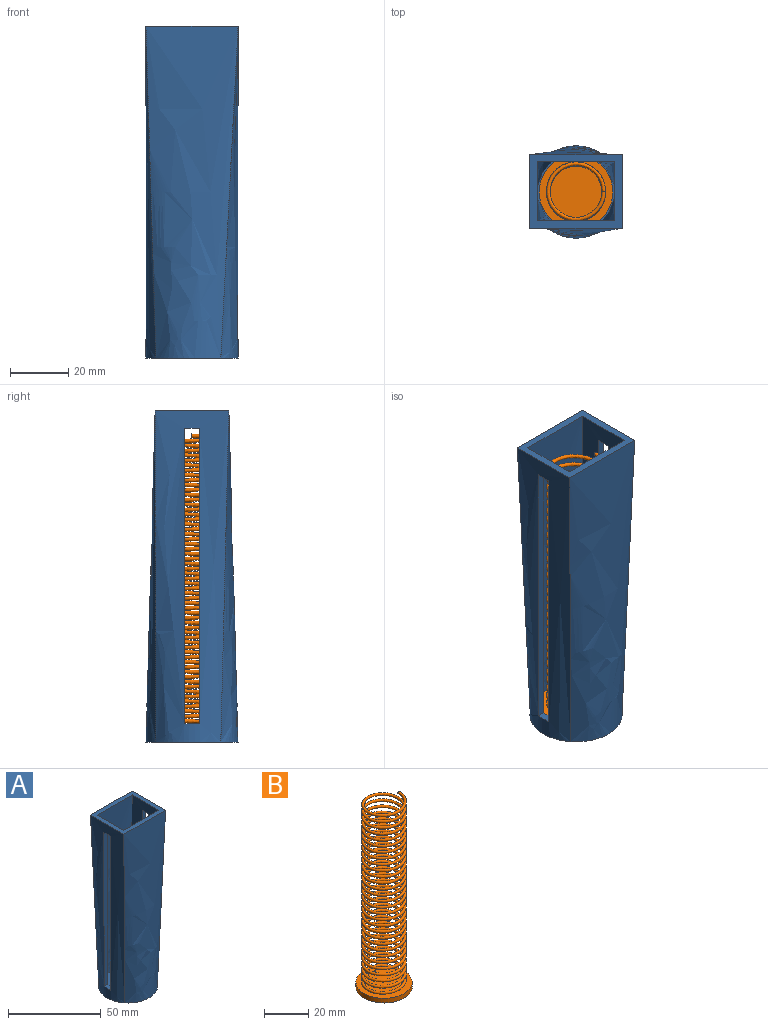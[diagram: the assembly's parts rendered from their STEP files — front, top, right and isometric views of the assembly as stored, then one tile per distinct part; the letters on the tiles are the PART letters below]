
ASSEMBLY  parts=2 mates=1
PART A: 19 faces, bbox 37.1x37.1x120.5 mm
  f0: bspline ~114.3x25.4mm, area 2308.9mm2, adj f4,f5,f6,f7,f15,f16,f17,f18
  f1: bspline ~114.3x25.4mm, area 2308.9mm2, adj f4,f5,f6,f7,f11,f12,f13,f14
  f2: offset ~120.52x30.51mm, area 1765.8mm2, adj f5,f8,f9,f10,f15,f16,f17,f18
  f3: offset ~120.52x30.51mm, area 1765.8mm2, adj f5,f8,f9,f10,f11,f12,f13,f14
  f4: plane 31.81x31.81mm, normal (0,0,-1), area 791.7mm2, adj f0,f1,f6,f7
  f5: plane 31.9x25.55mm, normal (0,0,1), area 264.6mm2, adj f0,f1,f2,f3,f6,f7,f9,f10
  f6: bspline ~115.44x31.84mm, area 3182.9mm2, adj f0,f1,f4,f5
  f7: bspline ~115.44x31.84mm, area 3182.9mm2, adj f0,f1,f4,f5
  f8: plane 27.01x26.86mm, normal (0,0,1), area 559.3mm2, adj f2,f3,f9,f10
  f9: offset ~120.52x36.92mm, area 2672.2mm2, adj f2,f3,f5,f8
  f10: offset ~120.52x36.92mm, area 2672.2mm2, adj f2,f3,f5,f8
  f11: plane 5.1x2.8mm, normal (0,0,1), area 13mm2, adj f1,f3,f12,f14
  f12: plane 101.69x2.85mm, normal (0,1,0), area 259.8mm2, adj f1,f3,f11,f13
  f13: plane 5.09x2.58mm, normal (0,0,-1), area 12.9mm2, adj f1,f3,f12,f14
  f14: plane 101.77x2.92mm, normal (0,-1,0), area 258.8mm2, adj f1,f3,f11,f13
  f15: plane 101.69x2.85mm, normal (0,-1,0), area 259.8mm2, adj f0,f2,f16,f18
  f16: plane 5.09x2.58mm, normal (0,0,-1), area 12.9mm2, adj f0,f2,f15,f17
  f17: plane 101.77x2.92mm, normal (0,1,0), area 258.8mm2, adj f0,f2,f16,f18
  f18: plane 5.1x2.8mm, normal (0,0,1), area 13mm2, adj f0,f2,f15,f17
PART B: 8 faces, bbox 25.6x25.6x103.7 mm
  f0: plane 1.45x1.45mm, normal (0,1,0), area 1.3mm2, adj f1
  f1: bspline ~102.23x20.29mm, area 7087.4mm2, adj f0,f3
  f2: cylinder r=12.7mm len=25.4mm, axis (0,0,-1), area 202.7mm2, adj f3,f6
  f3: plane 25.4x25.4mm, normal (0,0,1), area 475.7mm2, adj f1,f2
  f4: plane 1.45x1.45mm, normal (0,1,0), area 1mm2, adj f5,f6,f7
  f5: extruded ~8.81x6.59mm, area 28.9mm2, adj f4,f6,f7
  f6: plane 25.44x25.44mm, normal (0,0,-1), area 490.4mm2, adj f2,f4,f5
  f7: bspline ~9.43x6.85mm, area 14.2mm2, adj f4,f5
PLACE A t=(-19.84,27.79,-22.66)mm
PLACE B t=(-19.84,27.79,-18.85)mm
MATE fastened B.f2 <-> A.f8  axis (0,0,-1) through (-19.84,27.79,-20.12)mm
